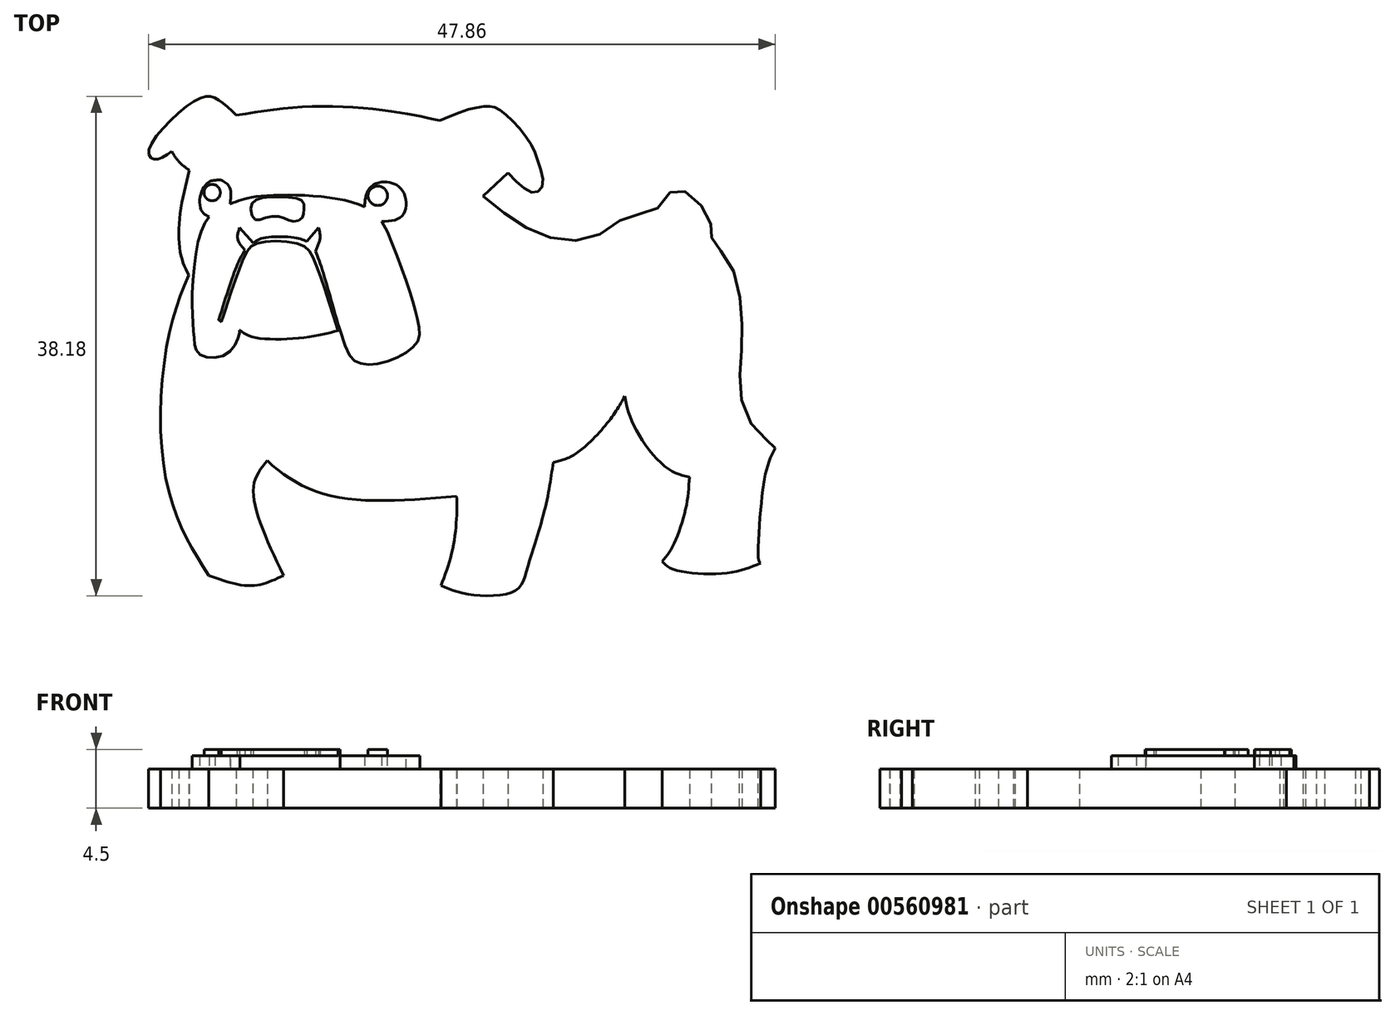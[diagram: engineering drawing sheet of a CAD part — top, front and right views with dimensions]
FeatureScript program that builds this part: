
annotation { "Feature Type Name" : "Feature", "Feature Type Description" : "" }
export const myFeature = defineFeature(function(context is Context, id is Id, definition is map)
    precondition{}
    {
        {
            var Q0;
            Q0=qCreatedBy(makeId("Top.planeOp"),FACE);
            var sketch = newSketch(context, id + "F0", { "sketchPlane" : qUnion([Q0])});
            skFitSpline(sketch, "E0", {"points": [v(2.37, 7.22) * mm, v(5.22, 5.07) * mm, v(8.21, 3.88) * mm, v(11.26, 4.28) * mm, v(13.55, 5.72) * mm, v(15.45, 6.07) * mm, v(16.7, 7.52) * mm, v(17.8, 7.57) * mm, v(19.4, 5.97) * mm, v(19.84, 4.48) * mm, v(19.9, 3.83) * mm, v(21.14, 2.23) * mm, v(22.04, -1.06) * mm, v(22.14, -4.46) * mm, v(22, -7.47) * mm, v(23, -10.4) * mm, v(24.43, -11.75) * mm, v(24.68, -12.05) * mm], "startDerivative": vector(37.04, -30.57) * mm, "endDerivative": vector(7.3, -10.5) * mm});
            skFitSpline(sketch, "E1", {"points": [v(24.68, -12.05) * mm, v(24.09, -13.47) * mm, v(23.59, -16.66) * mm, v(23.46, -20.73) * mm, v(23.59, -20.84) * mm], "startDerivative": vector(-2.8, -5.83) * mm, "endDerivative": vector(1.86, -0.5) * mm});
            skFitSpline(sketch, "E2", {"points": [v(23.59, -20.84) * mm, v(20.92, -21.62) * mm, v(16.87, -21.3) * mm, v(16.07, -20.73) * mm], "startDerivative": vector(-6.53, -2.77) * mm, "endDerivative": vector(-2.65, 2.9) * mm});
            skFitSpline(sketch, "E3", {"points": [v(16.07, -20.73) * mm, v(16.84, -19.58) * mm, v(17.84, -16.76) * mm, v(18.14, -14.27) * mm], "startDerivative": vector(2.93, 3.74) * mm, "endDerivative": vector(0.42, 6.78) * mm});
            skFitSpline(sketch, "E4", {"points": [v(18.14, -14.27) * mm, v(16.44, -13.6) * mm, v(13.96, -10.47) * mm, v(13.18, -8.1) * mm], "startDerivative": vector(-5.97, 1.28) * mm, "endDerivative": vector(-1.51, 6.96) * mm});
            skFitSpline(sketch, "E5", {"points": [v(13.18, -8.1) * mm, v(12.06, -9.88) * mm, v(9.45, -12.49) * mm, v(7.72, -13.14) * mm], "startDerivative": vector(-3, -5.37) * mm, "endDerivative": vector(-5.73, -1.3) * mm});
            skFitSpline(sketch, "E6", {"points": [v(-17.42, -9.3) * mm, v(-14.12, -13.02) * mm, v(-9.33, -15.69) * mm, v(0.35, -15.74) * mm], "startDerivative": vector(10.68, -13.38) * mm, "endDerivative": vector(26.04, 2.17) * mm});
            skFitSpline(sketch, "E7", {"points": [v(0.35, -15.74) * mm, v(0.35, -17.23) * mm, v(0, -19.98) * mm, v(-0.85, -22.57) * mm], "startDerivative": vector(0.14, -5.1) * mm, "endDerivative": vector(-2.62, -6.88) * mm});
            skFitSpline(sketch, "E8", {"points": [v(-0.85, -22.57) * mm, v(1.25, -23.22) * mm, v(4.8, -22.97) * mm, v(5.74, -21.28) * mm, v(7.09, -16.73) * mm, v(7.72, -13.14) * mm], "startDerivative": vector(10.76, -4.52) * mm, "endDerivative": vector(2.13, 15.7) * mm});
            skFitSpline(sketch, "E9", {"points": [v(6.24, -19.65) * mm, v(7.69, -19.73) * mm, v(9.47, -19.25) * mm, v(9.07, -17.05) * mm, v(10.42, -11.71) * mm], "startDerivative": vector(6.8, -0.73) * mm, "endDerivative": vector(6.34, 15.65) * mm});
            skFitSpline(sketch, "E10", {"points": [v(-14.12, -13.02) * mm, v(-15.18, -15.16) * mm, v(-12.88, -21.8) * mm], "startDerivative": vector(-4.07, -4.94) * mm, "endDerivative": vector(5.69, -12) * mm});
            skFitSpline(sketch, "E11", {"points": [v(-12.88, -21.8) * mm, v(-15.28, -22.57) * mm, v(-18.57, -21.8) * mm], "startDerivative": vector(-4.95, -2.4) * mm, "endDerivative": vector(-6.4, 2.3) * mm});
            skFitSpline(sketch, "E12", {"points": [v(-18.57, -21.8) * mm, v(-20.6, -18.29) * mm, v(-22.14, -12.49) * mm, v(-21.67, -3.57) * mm, v(-20.13, 1.18) * mm], "startDerivative": vector(-10.27, 15.9) * mm, "endDerivative": vector(7.44, 18.34) * mm});
            skFitSpline(sketch, "E13", {"points": [v(-11.09, 3.75) * mm, v(-10.19, 4.8) * mm], "startDerivative": vector(0.9, 1.05) * mm, "endDerivative": vector(0.9, 1.05) * mm});
            skFitSpline(sketch, "E14", {"points": [v(-10.44, 3) * mm, v(-10.09, 4) * mm, v(-10.19, 4.8) * mm], "startDerivative": vector(0.89, 1.91) * mm, "endDerivative": vector(-0.42, 1.68) * mm});
            skFitSpline(sketch, "E15", {"points": [v(-15.83, 3.1) * mm, v(-16.38, 3.95) * mm, v(-16.23, 4.8) * mm], "startDerivative": vector(-1.41, 1.6) * mm, "endDerivative": vector(0.64, 1.8) * mm});
            skFitSpline(sketch, "E16", {"points": [v(-16.23, 4.8) * mm, v(-15.18, 3.65) * mm], "startDerivative": vector(1.05, -1.15) * mm, "endDerivative": vector(1.05, -1.15) * mm});
            skCircle(sketch, "E17", {"center": v(-18.32, 7.49) * mm, "radius": 0.63 * mm});
            skFitSpline(sketch, "E18", {"points": [v(2.37, 7.22) * mm, v(4.28, 9) * mm], "startDerivative": vector(1.9, 1.77) * mm, "endDerivative": vector(1.9, 1.77) * mm});
            skFitSpline(sketch, "E19", {"points": [v(4.28, 9) * mm, v(6.15, 7.5) * mm, v(6.89, 7.93) * mm, v(6.64, 9.7) * mm, v(5.86, 11.46) * mm, v(4.28, 13.3) * mm, v(3.3, 14) * mm, v(2.68, 14.09) * mm, v(1.37, 13.88) * mm, v(-0.94, 12.99) * mm], "startDerivative": vector(14.52, -15.44) * mm, "endDerivative": vector(-17.49, -7.56) * mm});
            skFitSpline(sketch, "E20", {"points": [v(-0.94, 12.99) * mm, v(-4, 13.61) * mm, v(-10.33, 14.08) * mm, v(-16.48, 13.4) * mm], "startDerivative": vector(-10.53, 2.47) * mm, "endDerivative": vector(-16.25, -2.57) * mm});
            skFitSpline(sketch, "E21", {"points": [v(-16.48, 13.4) * mm, v(-18.01, 14.67) * mm, v(-19.5, 14.58) * mm, v(-23.16, 10.74) * mm, v(-22.75, 10.03) * mm, v(-21.4, 10.64) * mm], "startDerivative": vector(-7.83, 7.5) * mm, "endDerivative": vector(8.46, 5.78) * mm});
            skFitSpline(sketch, "E22", {"points": [v(-21.4, 10.64) * mm, v(-20.89, 9.86) * mm, v(-20.07, 9.2) * mm], "startDerivative": vector(0.96, -1.67) * mm, "endDerivative": vector(1.72, -1.23) * mm});
            skFitSpline(sketch, "E23", {"points": [v(-20.07, 9.2) * mm, v(-20.83, 5.38) * mm, v(-20.7, 2.64) * mm, v(-20.13, 1.18) * mm], "startDerivative": vector(-2.4, -9.62) * mm, "endDerivative": vector(2.53, -5.21) * mm});
            skFitSpline(sketch, "E24", {"points": [v(-15.83, 3.1) * mm, v(-15.18, 3.65) * mm, v(-14.34, 4.03) * mm, v(-11.96, 4.03) * mm, v(-11.09, 3.75) * mm, v(-10.44, 3) * mm, v(-8.12, -4.31) * mm, v(-7.16, -5.53) * mm, v(-5.52, -5.57) * mm, v(-3.3, -4.6) * mm, v(-2.5, -3.56) * mm, v(-2.67, -2.09) * mm, v(-3.25, 0) * mm, v(-4.64, 3.75) * mm, v(-6.78, 6.45) * mm, v(-14.55, 7.22) * mm, v(-16.48, 6.8) * mm, v(-17.72, 6.24) * mm, v(-18.98, 5) * mm, v(-19.85, -0.6) * mm, v(-19.71, -3.57) * mm, v(-19.29, -4.87) * mm, v(-17.14, -4.8) * mm, v(-16.23, -3.2) * mm, v(-16.23, -2.96) * mm], "startDerivative": vector(24.87, 22.16) * mm, "endDerivative": vector(-2.01, 12.86) * mm});
            skFitSpline(sketch, "E25", {"points": [v(-16.22, -3.02) * mm, v(-15.18, -3.57) * mm, v(-11.09, -3.57) * mm, v(-8.56, -3.02) * mm], "startDerivative": vector(3.44, -2.76) * mm, "endDerivative": vector(6.49, 1.81) * mm});
            skFitSpline(sketch, "E26", {"points": [v(-15.83, 3.1) * mm, v(-16.41, 1.95) * mm, v(-18.06, -3.02) * mm], "startDerivative": vector(-1.65, -2.8) * mm, "endDerivative": vector(-2.7, -8.77) * mm});
            skFitSpline(sketch, "E27", {"points": [v(-16.22, -3.02) * mm, v(-17.2, -2.64) * mm, v(-17.83, -2.25) * mm], "startDerivative": vector(-1.93, 0.65) * mm, "endDerivative": vector(-1.25, 0.9) * mm});
            skCircle(sketch, "E28", {"center": v(-5.67, 7.24) * mm, "radius": 0.74 * mm});
            skFitSpline(sketch, "E29", {"points": [v(-4.95, 8.3) * mm, v(-4.05, 7.94) * mm, v(-3.5, 6.75) * mm, v(-3.93, 5.6) * mm, v(-5.37, 5.27) * mm], "startDerivative": vector(4.36, -0.88) * mm, "endDerivative": vector(-6.08, -0.33) * mm});
            skFitSpline(sketch, "E30", {"points": [v(-4.95, 8.3) * mm, v(-5.44, 8.3) * mm, v(-6.34, 7.77) * mm, v(-6.68, 6.4) * mm], "startDerivative": vector(-1.83, 0.23) * mm, "endDerivative": vector(-0.29, -3.75) * mm});
            skFitSpline(sketch, "E31", {"points": [v(-18.12, 8.43) * mm, v(-17.63, 8.43) * mm, v(-17, 7.88) * mm, v(-16.95, 6.6) * mm], "startDerivative": vector(1.84, 0.3) * mm, "endDerivative": vector(-0.41, -3.4) * mm});
            skFitSpline(sketch, "E32", {"points": [v(-18.12, 8.43) * mm, v(-18.5, 8.34) * mm, v(-19.16, 7.5) * mm, v(-19.13, 6.08) * mm, v(-18.54, 5.65) * mm], "startDerivative": vector(-2.13, -0.1) * mm, "endDerivative": vector(2.94, -1.24) * mm});
            skFitSpline(sketch, "E33", {"points": [v(-15.02, 5.4) * mm, v(-14.15, 5.6) * mm, v(-12.94, 5.6) * mm, v(-12.2, 5.28) * mm, v(-11.5, 5.5) * mm, v(-11.33, 6.04) * mm, v(-11.38, 6.78) * mm, v(-12.48, 7.13) * mm, v(-14.7, 7.05) * mm, v(-15.37, 6.4) * mm, v(-15.02, 5.4) * mm]});
            skFitSpline(sketch, "E34", {"points": [v(-17.64, -2.39) * mm, v(-17.14, -0.93) * mm, v(-15.77, 2.8) * mm, v(-14.76, 3.65) * mm, v(-11.6, 3.52) * mm, v(-10.5, 2.25) * mm, v(-8.73, -3.07) * mm], "startDerivative": vector(3.32, 9.4) * mm, "endDerivative": vector(7.98, -25.68) * mm});
            skSolve(sketch);
        }
        {
            var Q0;
            Q0=makeQuery(id+"F0.imprint","IMPRINT",FACE,{"disambiguationData":[TD([[makeQuery(id+"F0.imprint","IMPRINT",EDGE,{"derivedFrom":sQuery(id+"F0.wireOp",EDGE,"E0")}),-1.0]])]});
            extrude(context, id + "F1", {"entities" : qUnion([Q0]), "depth" : 3 * mm, "offsetDistance" : 25 * mm});
        }
        {
            var Q0;
            {var subQ2=sQuery(id+"F0.wireOp",EDGE,"E25");Q0=makeQuery(id+"F0.imprint","IMPRINT",FACE,{"disambiguationData":[TD([[makeQuery(id+"F0.imprint","IMPRINT",EDGE,{"derivedFrom":subQ2}),1.0]])]});}
            var Q1;
            {var subQ6=sQuery(id+"F0.wireOp",EDGE,"E13");Q1=makeQuery(id+"F0.imprint","IMPRINT",FACE,{"disambiguationData":[TD([[makeQuery(id+"F0.imprint","IMPRINT",EDGE,{"derivedFrom":subQ6}),1.0]])]});}
            var Q2;
            Q2=makeQuery(id+"F0.imprint","IMPRINT",FACE,{"disambiguationData":[TD([[makeQuery(id+"F0.imprint","IMPRINT",EDGE,{"derivedFrom":sQuery(id+"F0.wireOp",EDGE,"E28")}),-1.0]])]});
            var Q3;
            Q3=makeQuery(id+"F0.imprint","IMPRINT",FACE,{"disambiguationData":[TD([[makeQuery(id+"F0.imprint","IMPRINT",EDGE,{"derivedFrom":sQuery(id+"F0.wireOp",EDGE,"E17")}),-1.0]])]});
            extrude(context, id + "F2", {"entities" : qUnion([Q0, Q1, Q2, Q3]), "operationType" : NewBodyOperationType.ADD, "depth" : 4 * mm, "offsetDistance" : 25 * mm});
        }
        {
            var Q0;
            Q0=makeQuery(id+"F0.imprint","IMPRINT",FACE,{"disambiguationData":[TD([[makeQuery(id+"F0.imprint","IMPRINT",EDGE,{"derivedFrom":sQuery(id+"F0.wireOp",EDGE,"E17")}),1.0]])]});
            var Q1;
            Q1=makeQuery(id+"F0.imprint","IMPRINT",FACE,{"disambiguationData":[TD([[makeQuery(id+"F0.imprint","IMPRINT",EDGE,{"derivedFrom":sQuery(id+"F0.wireOp",EDGE,"E28")}),1.0]])]});
            var Q2;
            Q2=makeQuery(id+"F0.imprint","IMPRINT",FACE,{"disambiguationData":[TD([[makeQuery(id+"F0.imprint","IMPRINT",EDGE,{"derivedFrom":sQuery(id+"F0.wireOp",EDGE,"E33")}),1.0]])]});
            var Q3;
            {var subQ0=sQuery(id+"F0.wireOp",EDGE,"E13");Q3=makeQuery(id+"F0.imprint","IMPRINT",FACE,{"disambiguationData":[TD([[makeQuery(id+"F0.imprint","IMPRINT",EDGE,{"derivedFrom":subQ0}),-1.0]])]});}
            var Q4;
            {var subQ0=sQuery(id+"F0.wireOp",EDGE,"E15");Q4=makeQuery(id+"F0.imprint","IMPRINT",FACE,{"disambiguationData":[TD([[makeQuery(id+"F0.imprint","IMPRINT",EDGE,{"derivedFrom":subQ0}),-1.0]])]});}
            extrude(context, id + "F3", {"entities" : qUnion([Q0, Q1, Q2, Q3, Q4]), "operationType" : NewBodyOperationType.ADD, "depth" : 4.5 * mm, "offsetDistance" : 25 * mm});
        }
        {
            var Q0;
            {var subQ0=sQuery(id+"F0.wireOp",EDGE,"E24");var subQ9=makeQuery(id+"F0.imprint","INTERSECT",VERTEX,{"derivedFrom":[sQuery(id+"F0.wireOp",EDGE,"E13"),subQ0]});Q0=makeQuery(id+"F0.imprint","IMPRINT",FACE,{"disambiguationData":[TD([[makeQuery(id+"F0.imprint","IMPRINT",EDGE,{"disambiguationData":[TD([[subQ9,1.0]])],"derivedFrom":subQ0}),-1.0]])]});}
            extrude(context, id + "F4", {"entities" : qUnion([Q0]), "operationType" : NewBodyOperationType.ADD, "depth" : 4.5 * mm, "offsetDistance" : 25 * mm});
        }
    });
